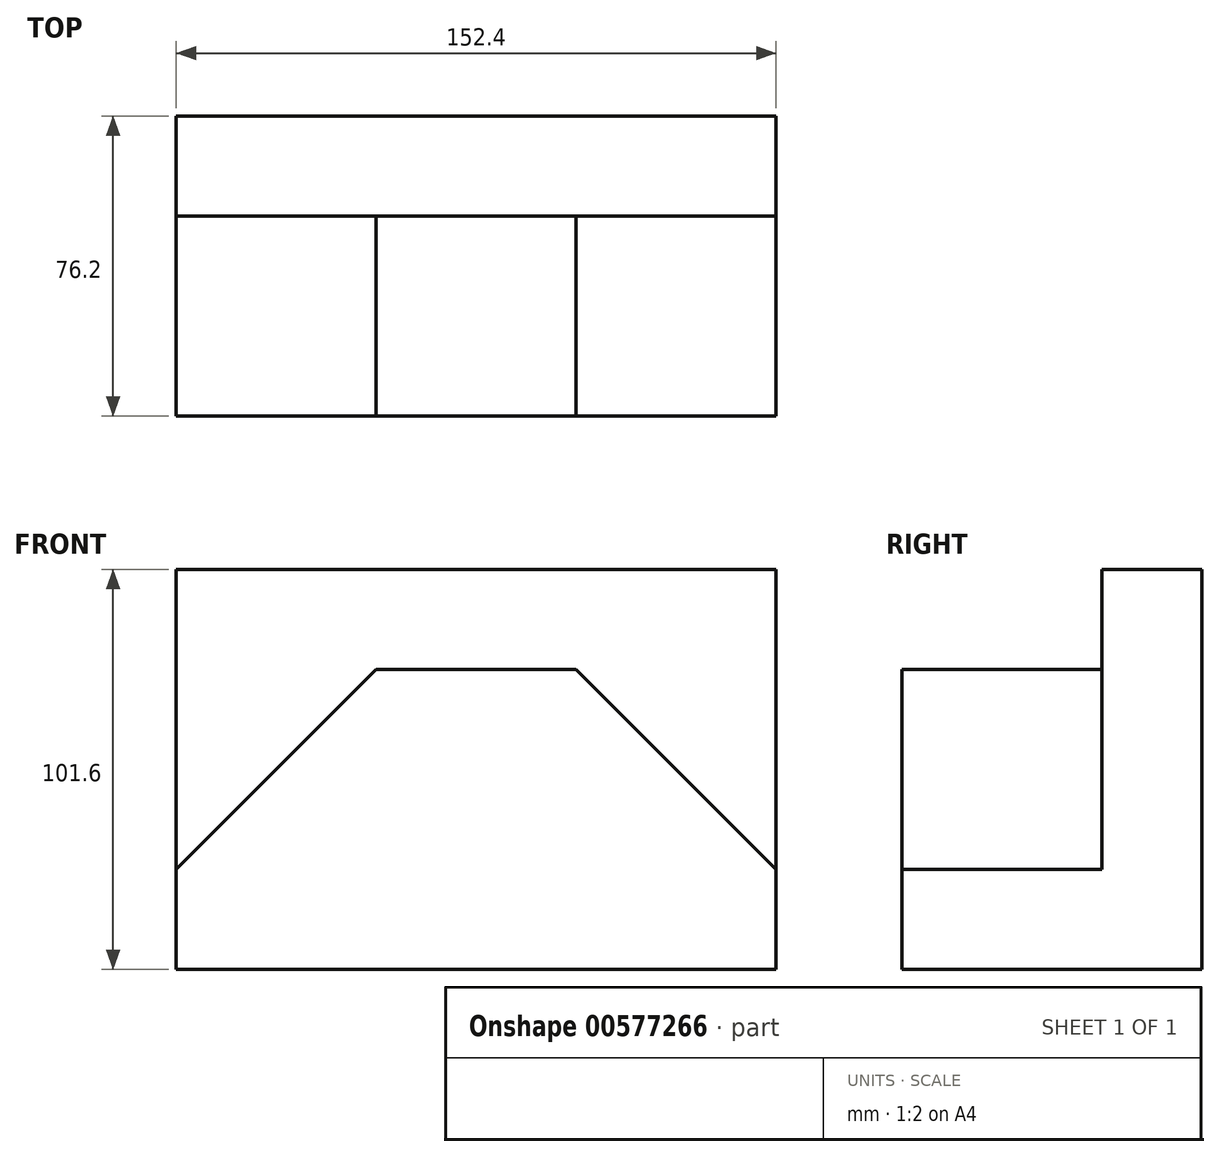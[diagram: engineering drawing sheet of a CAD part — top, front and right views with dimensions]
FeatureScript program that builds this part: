
annotation { "Feature Type Name" : "Feature", "Feature Type Description" : "" }
export const myFeature = defineFeature(function(context is Context, id is Id, definition is map)
    precondition{}
    {
        {
            var Q0;
            Q0=qCreatedBy(makeId("Top.planeOp"),FACE);
            var sketch = newSketch(context, id + "F0", { "sketchPlane" : qUnion([Q0])});
            skLineSegment(sketch, "E0.bottom", {"start": v(-72.39, 1) * mm, "end": v(80.01, 1) * mm});
            skLineSegment(sketch, "E0.top", {"start": v(-72.39, -75.2) * mm, "end": v(80.01, -75.2) * mm});
            skLineSegment(sketch, "E0.left", {"start": v(-72.39, 1) * mm, "end": v(-72.39, -75.2) * mm});
            skLineSegment(sketch, "E0.right", {"start": v(80.01, 1) * mm, "end": v(80.01, -75.2) * mm});
            skSolve(sketch);
        }
        {
            var Q0;
            Q0=makeQuery(id+"F0.imprint","IMPRINT",FACE,{"disambiguationData":[TD([[makeQuery(id+"F0.imprint","IMPRINT",EDGE,{"derivedFrom":sQuery(id+"F0.wireOp",EDGE,"E0.bottom")}),-1.0]])]});
            extrude(context, id + "F1", {"entities" : qUnion([Q0]), "depth" : 101.6 * mm, "offsetDistance" : 25.4 * mm});
        }
        {
            var Q0;
            Q0=makeQuery(id+"F1.opExtrude","SWEPT_FACE",FACE,{"disambiguationData":[OSD([sQuery(id+"F0.wireOp",EDGE,"E0.top")])]});
            var sketch = newSketch(context, id + "F2", { "sketchPlane" : qUnion([Q0])});
            skLineSegment(sketch, "E1.bottom", {"start": v(80.01, 25.4) * mm, "end": v(-72.39, 25.4) * mm});
            skLineSegment(sketch, "E1.top", {"start": v(80.01, 0) * mm, "end": v(-72.39, 0) * mm});
            skLineSegment(sketch, "E1.left", {"start": v(80.01, 25.4) * mm, "end": v(80.01, 0) * mm});
            skLineSegment(sketch, "E1.right", {"start": v(-72.39, 25.4) * mm, "end": v(-72.39, 0) * mm});
            skLineSegment(sketch, "E2.bottom", {"start": v(-72.39, 25.4) * mm, "end": v(-21.59, 25.4) * mm});
            skLineSegment(sketch, "E2.top", {"start": v(-72.39, 0) * mm, "end": v(-21.59, 0) * mm});
            skLineSegment(sketch, "E2.right", {"start": v(-21.59, 25.4) * mm, "end": v(-21.59, 0) * mm});
            skLineSegment(sketch, "E3.bottom", {"start": v(80.01, 25.4) * mm, "end": v(29.21, 25.4) * mm});
            skLineSegment(sketch, "E3.top", {"start": v(80.01, 0) * mm, "end": v(29.21, 0) * mm});
            skLineSegment(sketch, "E3.right", {"start": v(29.21, 25.4) * mm, "end": v(29.21, 0) * mm});
            skLineSegment(sketch, "E4.bottom", {"start": v(-21.59, 25.4) * mm, "end": v(29.21, 25.4) * mm});
            skLineSegment(sketch, "E4.top", {"start": v(-21.59, 0) * mm, "end": v(29.21, 0) * mm});
            skLineSegment(sketch, "E5.bottom", {"start": v(29.21, 25.4) * mm, "end": v(-21.59, 25.4) * mm});
            skLineSegment(sketch, "E5.top", {"start": v(29.21, 76.2) * mm, "end": v(-21.59, 76.2) * mm});
            skLineSegment(sketch, "E5.left", {"start": v(29.21, 25.4) * mm, "end": v(29.21, 76.2) * mm});
            skLineSegment(sketch, "E5.right", {"start": v(-21.59, 25.4) * mm, "end": v(-21.59, 76.2) * mm});
            skLineSegment(sketch, "E6", {"start": v(29.21, 76.2) * mm, "end": v(80.01, 25.4) * mm});
            skLineSegment(sketch, "E7", {"start": v(-21.59, 76.2) * mm, "end": v(-72.39, 25.4) * mm});
            skSolve(sketch);
        }
        {
            var Q0;
            Q0=makeQuery(id+"F2.imprint","IMPRINT",FACE,{"disambiguationData":[TD([[makeQuery(id+"F2.imprint","IMPRINT",EDGE,{"derivedFrom":sQuery(id+"F2.wireOp",EDGE,"E5.top")}),-1.0]])]});
            extrude(context, id + "F3", {"entities" : qUnion([Q0]), "operationType" : NewBodyOperationType.REMOVE, "oppositeDirection" : true, "depth" : 50.8 * mm, "offsetDistance" : 25.4 * mm});
        }
    });
